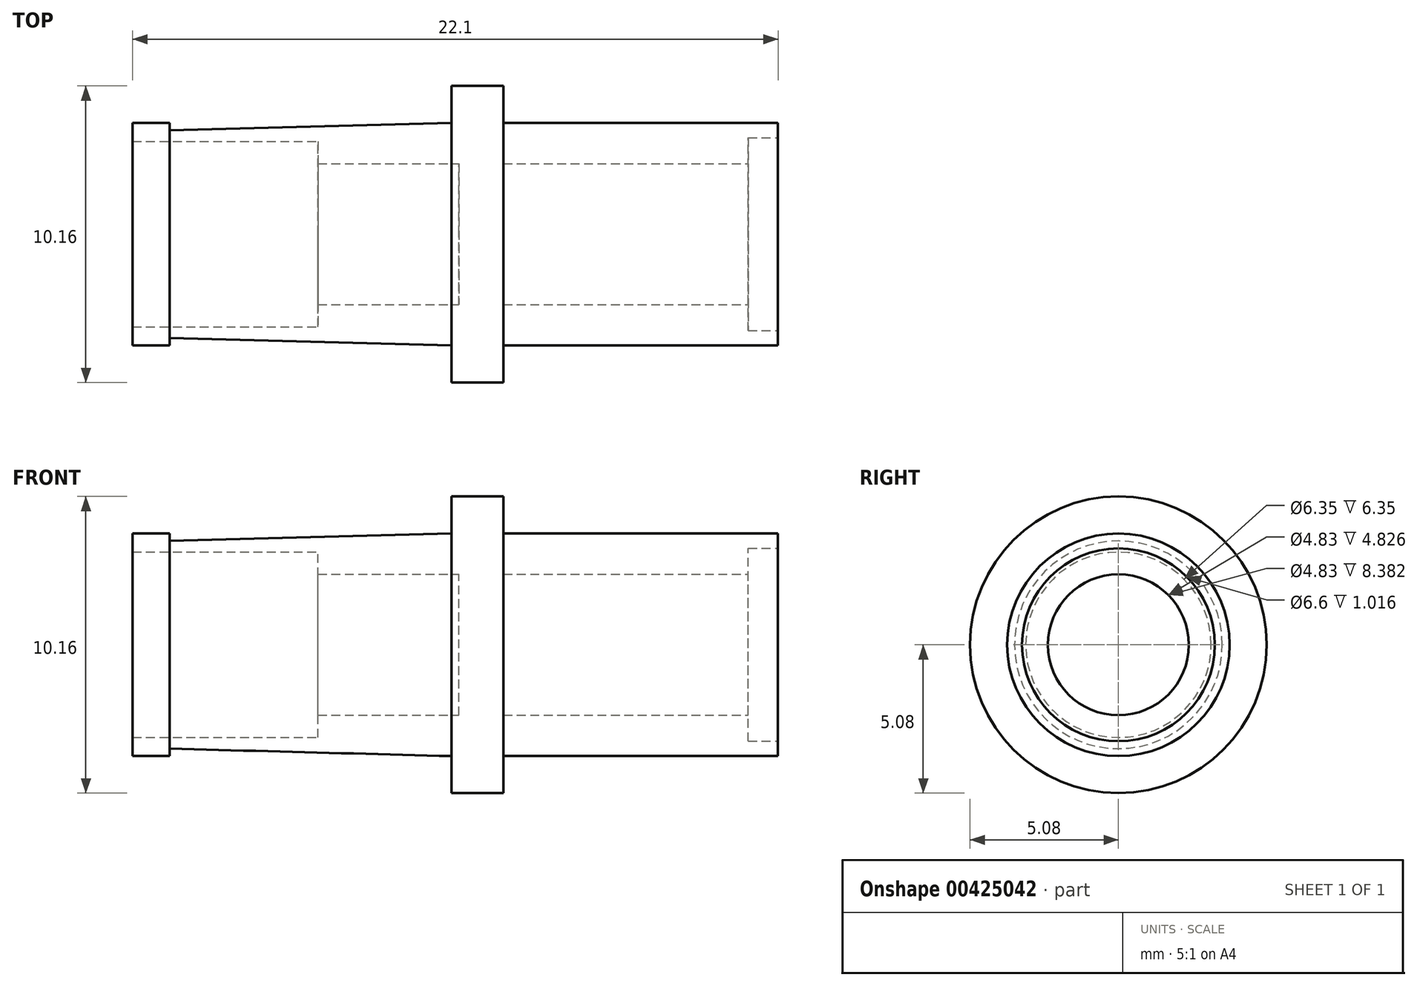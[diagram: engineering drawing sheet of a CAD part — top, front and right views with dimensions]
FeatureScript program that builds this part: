
annotation { "Feature Type Name" : "Feature", "Feature Type Description" : "" }
export const myFeature = defineFeature(function(context is Context, id is Id, definition is map)
    precondition{}
    {
        {
            var Q0;
            Q0=qCreatedBy(makeId("Front.planeOp"),FACE);
            var sketch = newSketch(context, id + "F0", { "sketchPlane" : qUnion([Q0])});
            skLineSegment(sketch, "E0", {"start": v(0, 0) * mm, "end": v(0, 1.27) * mm});
            skLineSegment(sketch, "E1", {"start": v(0, 1.27) * mm, "end": v(1.78, 1.27) * mm});
            skLineSegment(sketch, "E2", {"start": v(1.78, 1.27) * mm, "end": v(1.78, 0) * mm});
            skLineSegment(sketch, "E3", {"start": v(1.78, 0) * mm, "end": v(11.18, 0) * mm});
            skLineSegment(sketch, "E4", {"start": v(11.18, 0) * mm, "end": v(11.18, -0.5) * mm});
            skLineSegment(sketch, "E5", {"start": v(11.18, -0.5) * mm, "end": v(10.16, -0.5) * mm});
            skLineSegment(sketch, "E6", {"start": v(10.16, -0.5) * mm, "end": v(10.16, -1.4) * mm});
            skLineSegment(sketch, "E7", {"start": v(10.16, -1.4) * mm, "end": v(1.78, -1.4) * mm});
            skLineSegment(sketch, "E8", {"start": v(1.78, -1.4) * mm, "end": v(1.78, -3.81) * mm});
            skLineSegment(sketch, "E9", {"start": v(1.78, -3.81) * mm, "end": v(0.25, -3.81) * mm});
            skLineSegment(sketch, "E10", {"start": v(0.25, -3.81) * mm, "end": v(0.25, -1.4) * mm});
            skLineSegment(sketch, "E11", {"start": v(0.25, -1.4) * mm, "end": v(-4.57, -1.4) * mm});
            skLineSegment(sketch, "E12", {"start": v(-4.57, -1.4) * mm, "end": v(-4.57, -0.63) * mm});
            skLineSegment(sketch, "E13", {"start": v(-4.57, -0.63) * mm, "end": v(-10.92, -0.64) * mm});
            skLineSegment(sketch, "E14", {"start": v(-10.92, -0.64) * mm, "end": v(-10.92, 0) * mm});
            skLineSegment(sketch, "E15", {"start": v(-10.92, 0) * mm, "end": v(-9.65, 0) * mm});
            skLineSegment(sketch, "E16", {"start": v(-9.65, 0) * mm, "end": v(-9.65, -0.25) * mm});
            skLineSegment(sketch, "E17", {"start": v(-9.65, -0.25) * mm, "end": v(0, 0) * mm});
            skSolve(sketch);
        }
        {
            var Q0;
            Q0=makeQuery(id+"F0.imprint","IMPRINT",FACE,{"disambiguationData":[TD([[makeQuery(id+"F0.imprint","IMPRINT",EDGE,{"derivedFrom":sQuery(id+"F0.wireOp",EDGE,"E0")}),-1.0]])]});
            var Q1;
            Q1=sQuery(id+"F0.wireOp",EDGE,"E9");
            revolve(context, id + "F1", {"entities" : qUnion([Q0]), "axis" : qUnion([Q1]), "revolveType" : RevolveType.FULL});
        }
    });
